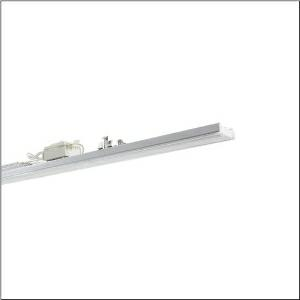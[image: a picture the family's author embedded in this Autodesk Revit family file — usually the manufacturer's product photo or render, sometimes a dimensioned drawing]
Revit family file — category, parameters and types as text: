
# Revit family: licross_21_recessed_mo_52tl10mn6axg
name_source: partatom
category: Lighting Fixtures
units: mm (PartAtom-declared; Revit-internal decimal feet)

## family parameters
Cut with Voids When Loaded = No
Host = Face
Light Source = No
Part Type = Normal
Room Calculation Point = No
Round Connector Dimension = Use Diameter
Shared = No

## types (1)
- --- (1 x LED, 10400 lm, 60.5 W, 6500K)
    Apparent Load = 61 VA
    CIE Flux Codes = 50 81 96 100 100
    Color Rendering = 80
    Color Temperature = 6500K
    Default Elevation = 1800 mm
    Description = Licross 21 Recessed MO, luminaire insert, of sheet steel, galvanised, coil coated, white, length: 1.500mm, width: 66mm, height: 67mm, LED rated luminous flux: 10.400lm, light colour: 865, SDCM (Standard Deviation of Colour Matching)MacAdam ≤ 3 SDCM (initial), control gear: ON/OFF Multilumen, with plug, 3-pole, with phase selection, mains connection: 220..240V, AC, 50/60Hz, rated input power: 61W, internal wiring halogen-free, primary optical cover: cover, of PMMA, light emission: direct distribution, primary light characteristic: symmetric, protection rating (complete): IP40, insulation class (complete): insulation class I (protective earthing), certification: CE, ENEC, VDE, UKCA, protection symbol: D if used in an environment without relevant dust loads with corresponding accessories, impact resistance: IK06, permissible ambient temperature for indoor applications: -35..+40°C, corresponds to IFS (International Featured Standards) requirements for safety and quality in the food industry, reducing of maximum allowable ambient temperature of 5°C with ceiling mounting, LABS conformity tested according to VDMA 24364:2018-05, The light source and the operating device comply with the requirements of the Ecodesign Regulation (EU) 2019/2020 and are replaceable in accordance with this regulation, packaging unit: 1 piece
    Height = 58 mm
    Lamp = 1 x LED
    Lamp Light Flux = 10400 lm
    Lamp Power = 60.5 W
    Lamp count = 1
    Length = 1500 mm
    Luminous efficacy = 172 lm/W
    Manufacturer = Siteco
    ModVariant = No
    Model = 52TL10MN6AXG
    Mounting Place = Ceiling
    Mounting Type = Pendant
    Number of Poles = 1
    OnlyDefault = Yes
    Power Factor = 1
    Product Name = Licross 21 Recessed MO
    Product group = luminaire insert | ceiling pendant
    ProductGroupID = 901
    Protection Class = Protection class I
    Protection Degree = IP 40
    RLX_Detail_Level = 1
    RLX_Emergency_Light_Flux = 0 lm
    RLX_Emergency_Type = 0
    RLX_Emergency_Type_DB = No
    RlxData = <blob elided: 22369 chars, md5=d14b18d9>
    Socket = socket
    Standby Power = 0 W
    System Light Flux = 10400 lm
    System Power = 61 W
    Type Comments = factory setting: luminous flux: 100 % | (A | C | E) | 140 mA
    Type Image = l_1296930.jpg
    URL = http://relux.com
    VarID = @adj_056015
    Voltage = 0 V
    Weight = 0.00 kg
    Width = 66 mm

## geometry (parser evidence)
native form markers: Blend x4, Sweep x11
no freeform markers — native parametric forms only
